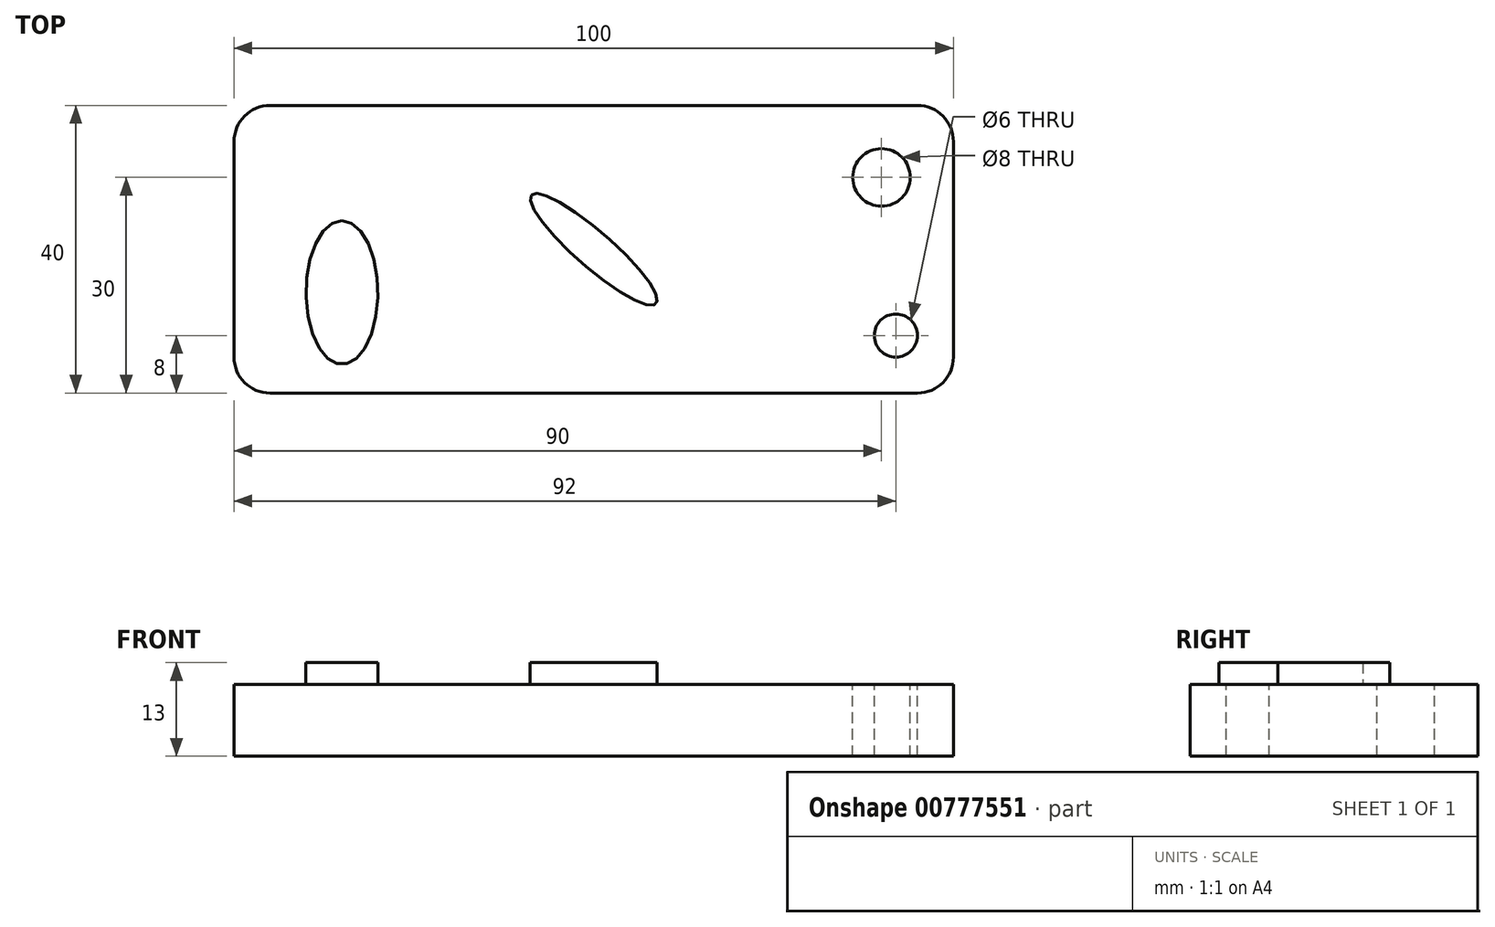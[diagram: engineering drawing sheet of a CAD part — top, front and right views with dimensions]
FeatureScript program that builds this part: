
annotation { "Feature Type Name" : "Feature", "Feature Type Description" : "" }
export const myFeature = defineFeature(function(context is Context, id is Id, definition is map)
    precondition{}
    {
        {
            var Q0;
            Q0=qCreatedBy(makeId("Top.planeOp"),FACE);
            var sketch = newSketch(context, id + "F0", { "sketchPlane" : qUnion([Q0])});
            skLineSegment(sketch, "E0.bottom", {"start": v(-50, 20) * mm, "end": v(50, 20) * mm});
            skLineSegment(sketch, "E0.top", {"start": v(-50, -20) * mm, "end": v(50, -20) * mm});
            skLineSegment(sketch, "E0.left", {"start": v(-50, 20) * mm, "end": v(-50, -20) * mm});
            skLineSegment(sketch, "E0.right", {"start": v(50, 20) * mm, "end": v(50, -20) * mm});
            skPoint(sketch, "E0.middle", {"position": v(0, 0) * mm});
            skSolve(sketch);
        }
        {
            var Q0;
            Q0 = qSketchRegion(id + "F0", true);
            extrude(context, id + "F1", {"entities" : qUnion([Q0]), "depth" : 10 * mm, "offsetDistance" : 25 * mm});
        }
        {
            var Q0;
            Q0=makeQuery(id+"F1.opExtrude","CAP_FACE",FACE,{"disambiguationData":[OSD([sQuery(id+"F0.wireOp",EDGE,"E0.bottom"),sQuery(id+"F0.wireOp",EDGE,"E0.top"),sQuery(id+"F0.wireOp",EDGE,"E0.left"),sQuery(id+"F0.wireOp",EDGE,"E0.right")])],"isStart":false});
            var sketch = newSketch(context, id + "F2", { "sketchPlane" : qUnion([Q0])});
            skEllipse(sketch, "E1", {"center": v(-35, -6) * mm, "majorRadius": 10 * mm, "minorRadius": 5 * mm, "majorAxis": v(0, 1)});
            skEllipse(sketch, "E2", {"center": v(0, 0) * mm, "majorRadius": 11.5 * mm, "minorRadius": 2.5 * mm, "majorAxis": v(-0.75, 0.66)});
            skSolve(sketch);
        }
        {
            var Q0;
            Q0 = qSketchRegion(id + "F2", true);
            extrude(context, id + "F3", {"entities" : qUnion([Q0]), "operationType" : NewBodyOperationType.ADD, "depth" : 3 * mm, "offsetDistance" : 25 * mm});
        }
        {
            var Q0;
            Q0=makeQuery(id+"F1.opExtrude","CAP_FACE",FACE,{"disambiguationData":[OSD([sQuery(id+"F0.wireOp",EDGE,"E0.bottom"),sQuery(id+"F0.wireOp",EDGE,"E0.top"),sQuery(id+"F0.wireOp",EDGE,"E0.left"),sQuery(id+"F0.wireOp",EDGE,"E0.right")])],"isStart":false});
            var sketch = newSketch(context, id + "F4", { "sketchPlane" : qUnion([Q0])});
            skCircle(sketch, "E3", {"center": v(40, 10) * mm, "radius": 4 * mm});
            skCircle(sketch, "E4", {"center": v(42, -12) * mm, "radius": 3 * mm});
            skSolve(sketch);
        }
        {
            var Q0;
            Q0 = qSketchRegion(id + "F4", true);
            extrude(context, id + "F5", {"entities" : qUnion([Q0]), "operationType" : NewBodyOperationType.REMOVE, "oppositeDirection" : true, "depth" : 10 * mm, "offsetDistance" : 25 * mm});
        }
        {
            var Q0;
            Q0=makeQuery(id+"F1.opExtrude","SWEPT_EDGE",EDGE,{"disambiguationData":[OSD([sQuery(id+"F0.wireOp",EDGE,"E0.top"),sQuery(id+"F0.wireOp",EDGE,"E0.left")])]});
            var Q1;
            Q1=makeQuery(id+"F1.opExtrude","SWEPT_EDGE",EDGE,{"disambiguationData":[OSD([sQuery(id+"F0.wireOp",EDGE,"E0.bottom"),sQuery(id+"F0.wireOp",EDGE,"E0.left")])]});
            var Q2;
            Q2=makeQuery(id+"F1.opExtrude","SWEPT_EDGE",EDGE,{"disambiguationData":[OSD([sQuery(id+"F0.wireOp",EDGE,"E0.bottom"),sQuery(id+"F0.wireOp",EDGE,"E0.right")])]});
            var Q3;
            Q3=makeQuery(id+"F1.opExtrude","SWEPT_EDGE",EDGE,{"disambiguationData":[OSD([sQuery(id+"F0.wireOp",EDGE,"E0.top"),sQuery(id+"F0.wireOp",EDGE,"E0.right")])]});
            fillet(context, id + "F6", {"entities" : qUnion([Q0, Q1, Q2, Q3]), "radius" : 5 * mm, "tangentPropagation" : true, "allowEdgeOverflow" : false});
        }
    });
